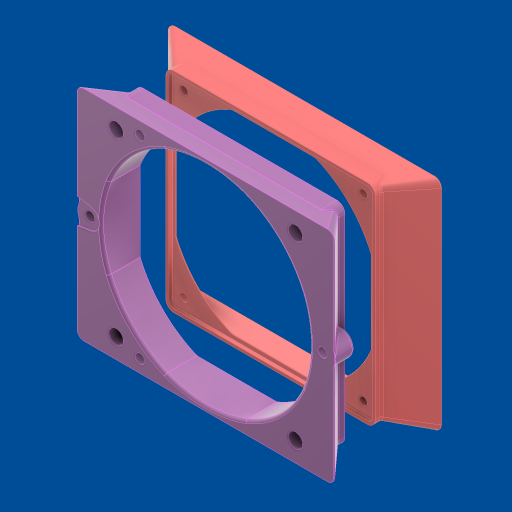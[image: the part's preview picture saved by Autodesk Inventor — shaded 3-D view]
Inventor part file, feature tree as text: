
AUTODESK INVENTOR PART (.ipt)
format: ipt  version: 2023.2 (Build 272271000, 271)  size: 2,375,168 bytes
history: native  units: mm
features: sketch x9, other x6, extrude x5, fillet x5, plane x4, loft x4, hole x3, projected_geometry x2, helix x1
ambient origin geometry x8: Origin, YZ Plane, XZ Plane, XY Plane, X Axis, Y Axis, Z Axis, Center Point
bodies: Body1 (feature_tree), Body2 (feature_tree), Body3 (feature_tree)
feature tree (39):
  other  "nf-a14.ipt"
  plane  "Work Plane2"
  sketch  "Sketch1"  dims[d0=10.0mm d1=34.5mm d2=-69.0mm]
  sketch  "Sketch2"  dims[d8=162.0mm d30=5.0mm]
  sketch  "Sketch3"  dims[d35=134.0mm d36=9.740359mm]
  sketch  "Sketch4"  dims[d37=9.740359mm d38=145.0mm]
  loft  "Loft1"
  loft  "Loft2"
  hole  "Hole1"  [1 undecoded]
  loft  "Loft3"
  loft  "Loft4"
  hole  "Hole2"  [1 undecoded]
  hole  "Hole3"  [1 undecoded]
  extrude  "Extrusion1"  TaperAngle=0.0deg  [1 undecoded]
  extrude  "Extrusion2"  TaperAngle=0.0deg  [1 undecoded]
  extrude  "Extrusion3"  TaperAngle=0.0deg  [1 undecoded]
  plane  "Work Plane3"
  extrude  "Extrusion4"  TaperAngle=0.0deg  [1 undecoded]
  plane  "Work Plane4"
  extrude  "Extrusion5"  TaperAngle=0.0deg  [1 undecoded]
  fillet  "Fillet1"  [1 undecoded]
  fillet  "Fillet2"  Radius=14.0mm
  fillet  "Fillet3"  Radius=3.7mm
  fillet  "Fillet4"  Radius=1.0mm
  fillet  "Fillet5"  Radius=18.0mm
  other  "Solid1::nf-a14.ipt"
  other  "TaggingFeature1"
  plane  "Work Plane1"
  other  "Image2"
  projected_geometry  "Projected Loop1"
  helix  "coil_side"  [1 undecoded]
  other  "exhaust_side"
  sketch  "Sketch5"  dims[d42=20.0mm d45=1.0mm]
  sketch  "Sketch6"  dims[d46=5.0mm d47=190.0mm]
  sketch  "Sketch7"  dims[d48=5.0mm d49=2.0mm]
  sketch  "Sketch8"  dims[d50=0.0mm d51=90.0deg d52=0.0mm d53=90.0deg]
  sketch  "Sketch9"  dims[d54=0.0mm d55=90.0deg d56=0.0mm d57=90.0deg d58=5.5mm d59=10.0mm d60=10.0mm d61=18.0mm d62=90.0deg d63=8.0mm d64=20.594885mm d65=0.0mm d66=90.0deg d67=0.0mm d68=90.0deg d69=0.0mm d70=90.0deg d71=0.0mm d72=90.0deg d73=5.5mm d74=6.0mm d75=10.0mm d76=18.0mm d77=90.0deg d78=8.0mm d79=20.594885mm d80=6.5278mm d81=6.0mm d82=10.0mm d83=18.0mm d84=90.0deg d85=14.0mm d86=0.0mm d87=14.0mm d88=0.0mm d89=3.7mm d90=0.0mm d92=1.0mm d93=18.0mm d94=1.0mm d95=0.0mm d96=2.0mm d97=0.5mm d98=2.0mm d99=3.7mm d100=0.0mm d101=2.0mm d102=10.0mm d103=0.0mm d104=2.0mm d105=0.25mm d106=2.0mm d107=2.0mm d108=0.25mm]
  projected_geometry  "Projected Loop2"
  other  "fan"
note: 10 required parameter values undecoded (feature->parameter linkage not recoverable at this tier; creation-order binding heuristic only, values carry confidence <= 0.55)
